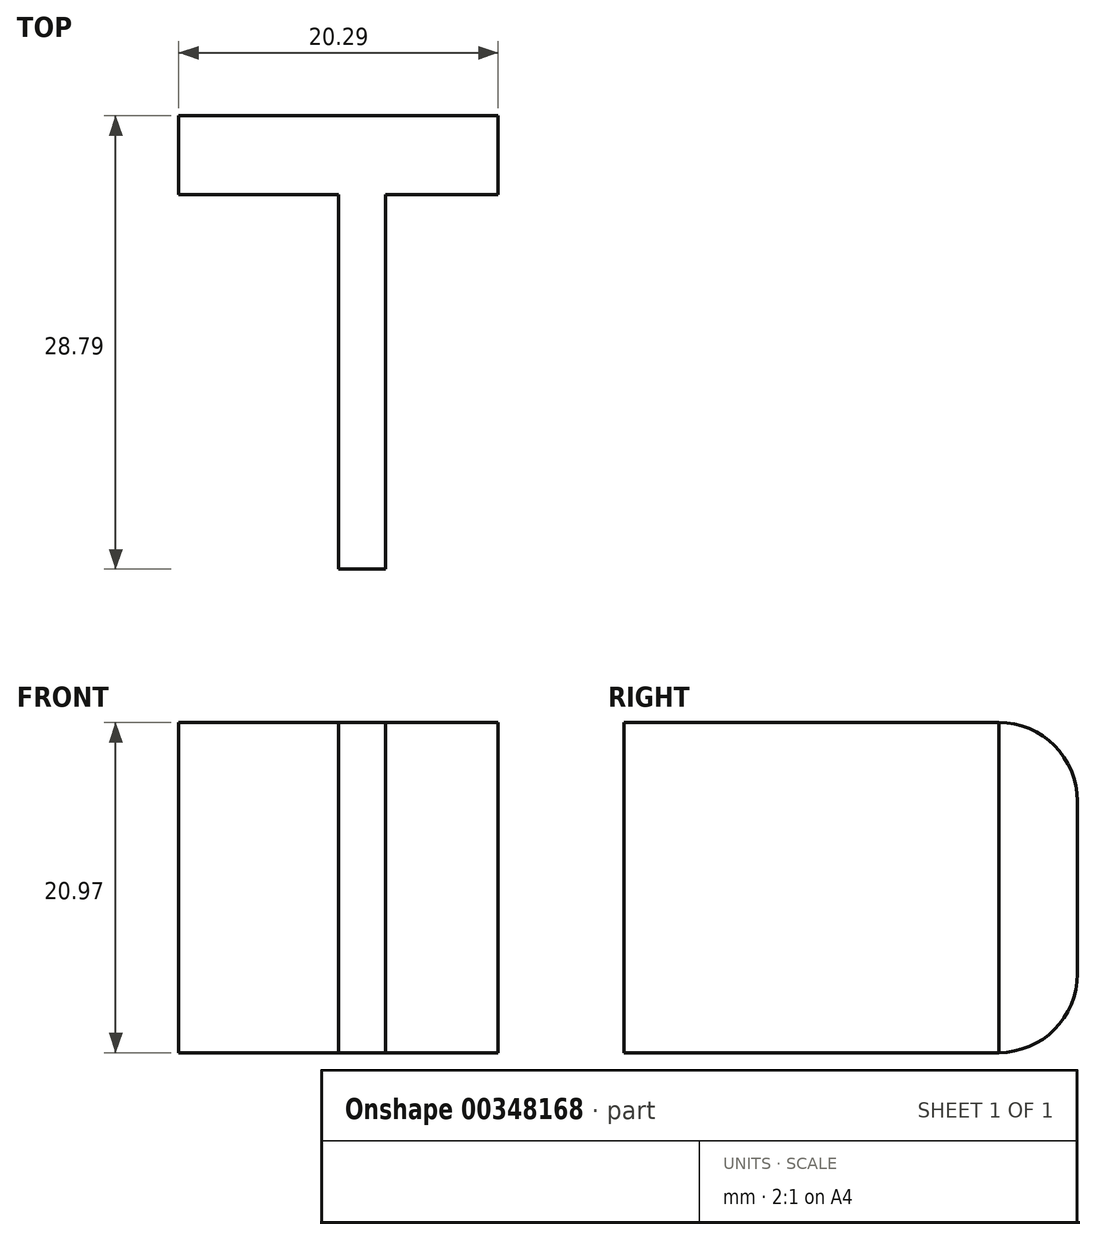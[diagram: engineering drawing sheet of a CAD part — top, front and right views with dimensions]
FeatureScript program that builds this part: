
annotation { "Feature Type Name" : "Feature", "Feature Type Description" : "" }
export const myFeature = defineFeature(function(context is Context, id is Id, definition is map)
    precondition{}
    {
        {
            var Q0;
            Q0=qCreatedBy(makeId("Front.planeOp"),FACE);
            var sketch = newSketch(context, id + "F0", { "sketchPlane" : qUnion([Q0])});
            skLineSegment(sketch, "E0.bottom", {"start": v(0, 37.13) * mm, "end": v(-20.29, 37.13) * mm});
            skLineSegment(sketch, "E0.top", {"start": v(0, 16.16) * mm, "end": v(-20.29, 16.16) * mm});
            skLineSegment(sketch, "E0.left", {"start": v(0, 37.13) * mm, "end": v(0, 16.16) * mm});
            skLineSegment(sketch, "E0.right", {"start": v(-20.29, 37.13) * mm, "end": v(-20.29, 16.16) * mm});
            skLineSegment(sketch, "E1.bottom", {"start": v(-10.14, 16.16) * mm, "end": v(-10.14, 16.16) * mm});
            skLineSegment(sketch, "E1.top", {"start": v(-10.14, 37.13) * mm, "end": v(-10.14, 37.13) * mm});
            skLineSegment(sketch, "E1.left", {"start": v(-10.14, 16.16) * mm, "end": v(-10.14, 37.13) * mm});
            skLineSegment(sketch, "E1.right", {"start": v(-10.14, 16.16) * mm, "end": v(-10.14, 37.13) * mm});
            skSolve(sketch);
        }
        {
            var Q0;
            Q0=sQuery(id+"F0.wireOp",EDGE,"E1.right");
            extrude(context, id + "F1", {"bodyType" : ToolBodyType.SURFACE, "surfaceEntities" : qUnion([Q0]), "depth" : 23.79 * mm});
        }
        {
            var Q0;
            Q0=makeQuery(id+"F1.opExtrude","SWEPT_FACE",FACE,{"disambiguationData":[OSD([sQuery(id+"F0.wireOp",EDGE,"E1.right")])]});
            extrude(context, id + "F2", {"entities" : qUnion([Q0]), "depth" : 3 * mm});
        }
        {
            var Q0;
            {var subQ0=sQuery(id+"F0.wireOp",EDGE,"E0.left");Q0=makeQuery(id+"F0.imprint","IMPRINT",FACE,{"disambiguationData":[TD([[makeQuery(id+"F0.imprint","IMPRINT",EDGE,{"derivedFrom":subQ0}),-1.0]])]});}
            var Q1;
            {var subQ0=sQuery(id+"F0.wireOp",EDGE,"E0.right");Q1=makeQuery(id+"F0.imprint","IMPRINT",FACE,{"disambiguationData":[TD([[makeQuery(id+"F0.imprint","IMPRINT",EDGE,{"derivedFrom":subQ0}),1.0]])]});}
            extrude(context, id + "F3", {"entities" : qUnion([Q0, Q1]), "operationType" : NewBodyOperationType.ADD, "oppositeDirection" : true, "depth" : 5 * mm});
        }
        {
            var Q0;
            Q0=makeQuery(id+"F3.opExtrude","CAP_EDGE",EDGE,{"disambiguationData":[OSD([sQuery(id+"F0.wireOp",EDGE,"E0.bottom")])],"isStart":false});
            fillet(context, id + "F4", {"entities" : qUnion([Q0]), "radius" : 5 * mm, "tangentPropagation" : true, "allowEdgeOverflow" : false});
        }
        {
            var Q0;
            Q0=makeQuery(id+"F3.opExtrude","CAP_EDGE",EDGE,{"disambiguationData":[OSD([sQuery(id+"F0.wireOp",EDGE,"E0.top")])],"isStart":false});
            fillet(context, id + "F5", {"entities" : qUnion([Q0]), "radius" : 5 * mm, "tangentPropagation" : true, "allowEdgeOverflow" : false});
        }
    });
